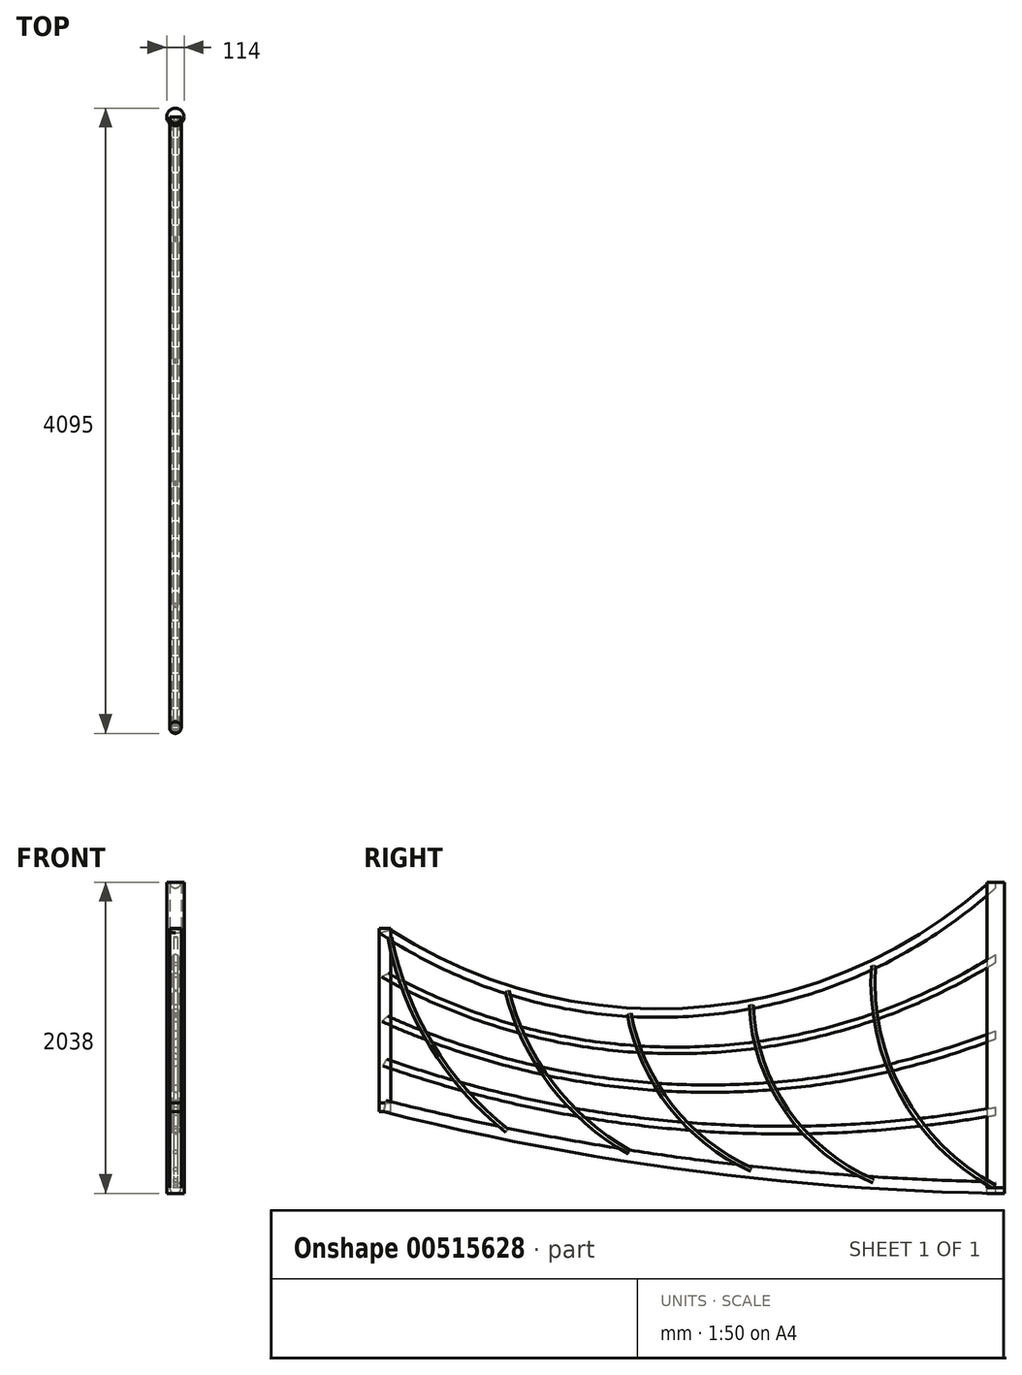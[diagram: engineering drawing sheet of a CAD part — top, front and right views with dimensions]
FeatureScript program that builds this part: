
annotation { "Feature Type Name" : "Feature", "Feature Type Description" : "" }
export const myFeature = defineFeature(function(context is Context, id is Id, definition is map)
    precondition{}
    {
        {
            var Q0;
            Q0=qCreatedBy(makeId("Right.planeOp"),FACE);
            var sketch = newSketch(context, id + "F0", { "sketchPlane" : qUnion([Q0])});
            skLineSegment(sketch, "E0.top", {"start": v(0, 2000) * mm, "end": v(-4000, 2000) * mm});
            skLineSegment(sketch, "E0.left", {"start": v(0, 0) * mm, "end": v(0, 2000) * mm});
            skLineSegment(sketch, "E0.right", {"start": v(-4000, 0) * mm, "end": v(-4000, 2000) * mm});
            skPoint(sketch, "E1", {"position": v(-4000, 533) * mm});
            skPoint(sketch, "E2", {"position": v(-4000, 819) * mm});
            skPoint(sketch, "E3", {"position": v(-4000, 1105) * mm});
            skPoint(sketch, "E4", {"position": v(-4000, 1678) * mm});
            skPoint(sketch, "E5", {"position": v(-4000, 178) * mm});
            skPoint(sketch, "E6", {"position": v(-4000, 1391) * mm});
            skPoint(sketch, "E7", {"position": v(0, 500) * mm});
            skPoint(sketch, "E8", {"position": v(0, 1000) * mm});
            skPoint(sketch, "E9", {"position": v(0, 1500) * mm});
            skPoint(sketch, "E10", {"position": v(0, 2000) * mm});
            skArc(sketch, "E11", {"start": v(-4000, 533) * mm, "mid": v(-2015.3, 151.64) * mm, "end": v(0, 0) * mm});
            skPoint(sketch, "E12", {"position": v(-2000, 0) * mm});
            skPoint(sketch, "E13", {"position": v(-2000, 649.6) * mm});
            skPoint(sketch, "E14", {"position": v(-2000, 899.6) * mm});
            skPoint(sketch, "E15", {"position": v(-2000, 1149.6) * mm});
            skPoint(sketch, "E16", {"position": v(-2000, 399.6) * mm});
            skLineSegment(sketch, "E17", {"start": v(-2000, 0) * mm, "end": v(-2000, 149.6) * mm});
            skArc(sketch, "E18", {"start": v(-4000, 819) * mm, "mid": v(-2020.6, 401.22) * mm, "end": v(0, 500) * mm});
            skArc(sketch, "E19", {"start": v(-4000, 1105) * mm, "mid": v(-2010.57, 649.87) * mm, "end": v(0, 1000) * mm});
            skArc(sketch, "E20", {"start": v(-4000, 1391) * mm, "mid": v(-1985.13, 899.98) * mm, "end": v(0, 1500) * mm});
            skArc(sketch, "E21", {"start": v(-4000, 1678) * mm, "mid": v(-1944.82, 1153.58) * mm, "end": v(0, 2000) * mm});
            skSolve(sketch);
        }
        {
            var Q0;
            Q0=qCreatedBy(makeId("Front.planeOp"),FACE);
            var sketch = newSketch(context, id + "F1", { "sketchPlane" : qUnion([Q0])});
            skCircle(sketch, "E22", {"center": v(0, 0) * mm, "radius": 38 * mm});
            skCircle(sketch, "E23", {"center": v(0, 500) * mm, "radius": 25.5 * mm});
            skCircle(sketch, "E24", {"center": v(0, 1000) * mm, "radius": 25.5 * mm});
            skCircle(sketch, "E25", {"center": v(0, 1500) * mm, "radius": 25.5 * mm});
            skCircle(sketch, "E26", {"center": v(0, 2000) * mm, "radius": 38 * mm});
            skSolve(sketch);
        }
        {
            var Q0;
            Q0=makeQuery(id+"F1.imprint","IMPRINT",FACE,{"disambiguationData":[TD([[makeQuery(id+"F1.imprint","IMPRINT",EDGE,{"derivedFrom":sQuery(id+"F1.wireOp",EDGE,"E22")}),1.0]])]});
            var Q1;
            Q1=sQuery(id+"F0.wireOp",EDGE,"E11");
            sweep(context, id + "F2", {"profiles" : qUnion([Q0]), "path" : qUnion([Q1])});
        }
        {
            var Q0;
            Q0=makeQuery(id+"F1.imprint","IMPRINT",FACE,{"disambiguationData":[TD([[makeQuery(id+"F1.imprint","IMPRINT",EDGE,{"derivedFrom":sQuery(id+"F1.wireOp",EDGE,"E23")}),1.0]])]});
            var Q1;
            Q1=sQuery(id+"F0.wireOp",EDGE,"E18");
            sweep(context, id + "F3", {"profiles" : qUnion([Q0]), "path" : qUnion([Q1])});
        }
        {
            var Q0;
            Q0=makeQuery(id+"F1.imprint","IMPRINT",FACE,{"disambiguationData":[TD([[makeQuery(id+"F1.imprint","IMPRINT",EDGE,{"derivedFrom":sQuery(id+"F1.wireOp",EDGE,"E24")}),1.0]])]});
            var Q1;
            Q1=sQuery(id+"F0.wireOp",EDGE,"E19");
            sweep(context, id + "F4", {"profiles" : qUnion([Q0]), "path" : qUnion([Q1])});
        }
        {
            var Q0;
            Q0=makeQuery(id+"F1.imprint","IMPRINT",FACE,{"disambiguationData":[TD([[makeQuery(id+"F1.imprint","IMPRINT",EDGE,{"derivedFrom":sQuery(id+"F1.wireOp",EDGE,"E25")}),1.0]])]});
            var Q1;
            Q1=sQuery(id+"F0.wireOp",EDGE,"E20");
            sweep(context, id + "F5", {"profiles" : qUnion([Q0]), "path" : qUnion([Q1])});
        }
        {
            var Q0;
            Q0=makeQuery(id+"F1.imprint","IMPRINT",FACE,{"disambiguationData":[TD([[makeQuery(id+"F1.imprint","IMPRINT",EDGE,{"derivedFrom":sQuery(id+"F1.wireOp",EDGE,"E26")}),1.0]])]});
            var Q1;
            Q1=sQuery(id+"F0.wireOp",EDGE,"E21");
            sweep(context, id + "F6", {"profiles" : qUnion([Q0]), "path" : qUnion([Q1])});
        }
        {
            var Q0;
            Q0=qCreatedBy(makeId("Top.planeOp"),FACE);
            var sketch = newSketch(context, id + "F7", { "sketchPlane" : qUnion([Q0])});
            skCircle(sketch, "E27", {"center": v(0, 0) * mm, "radius": 57 * mm});
            skSolve(sketch);
        }
        {
            var Q0;
            Q0=makeQuery(id+"F7.imprint","IMPRINT",FACE,{"disambiguationData":[TD([[makeQuery(id+"F7.imprint","IMPRINT",EDGE,{"derivedFrom":sQuery(id+"F7.wireOp",EDGE,"E27")}),1.0]])]});
            extrude(context, id + "F8", {"entities" : qUnion([Q0]), "depth" : 2000 * mm, "offsetDistance" : 25 * mm});
        }
        {
            var Q0;
            Q0=qCreatedBy(makeId("Top.planeOp"),FACE);
            cPlane(context, id + "F9", {"entities" : qUnion([Q0]), "cplaneType" : CPlaneType.OFFSET, "offset" : 553 * mm, "width" : 150 * mm, "height" : 150 * mm});
        }
        {
            var Q0;
            Q0=qCreatedBy(id+"F9.planeOp",FACE);
            var sketch = newSketch(context, id + "F10", { "sketchPlane" : qUnion([Q0])});
            skCircle(sketch, "E28", {"center": v(0, -4000) * mm, "radius": 38 * mm});
            skSolve(sketch);
        }
        {
            var Q0;
            Q0=makeQuery(id+"F10.imprint","IMPRINT",FACE,{"disambiguationData":[TD([[makeQuery(id+"F10.imprint","IMPRINT",EDGE,{"derivedFrom":sQuery(id+"F10.wireOp",EDGE,"E28")}),1.0]])]});
            extrude(context, id + "F11", {"entities" : qUnion([Q0]), "depth" : 1145 * mm, "offsetDistance" : 25 * mm});
        }
        {
            var Q0;
            Q0=makeQuery(id+"F6.opSweep","CAP_FACE",FACE,{"disambiguationData":[OSD([sQuery(id+"F0.wireOp",VERTEX,"E21.end"),sQuery(id+"F1.wireOp",EDGE,"E26")])],"isStart":true});
            var sketch = newSketch(context, id + "F12", { "sketchPlane" : qUnion([Q0])});
            skLineSegment(sketch, "E29.0", {"start": v(-57, 2000) * mm, "end": v(57, 2000) * mm});
            skLineSegment(sketch, "E30.top", {"start": v(-57, 2046.28) * mm, "end": v(57, 2046.28) * mm});
            skLineSegment(sketch, "E30.left", {"start": v(-57, 2000) * mm, "end": v(-57, 2046.28) * mm});
            skLineSegment(sketch, "E30.right", {"start": v(57, 2000) * mm, "end": v(57, 2046.28) * mm});
            skSolve(sketch);
        }
        {
            var Q0;
            {var subQ0=sQuery(id+"F12.wireOp",EDGE,"E29.0");var subQ1=makeQuery(id+"F6.opSweep","CAP_EDGE",EDGE,{"disambiguationData":[OSD([sQuery(id+"F0.wireOp",VERTEX,"E21.end"),sQuery(id+"F1.wireOp",EDGE,"E26")])],"isStart":true});var subQ2=makeQuery(id+"F12.imprint","INTERSECT",VERTEX,{"disambiguationData":[OD(0.0)],"derivedFrom":[subQ1,subQ0]});Q0=makeQuery(id+"F12.imprint","IMPRINT",FACE,{"disambiguationData":[TD([[makeQuery(id+"F12.imprint","IMPRINT",EDGE,{"disambiguationData":[TD([[subQ2,-1.0]])],"derivedFrom":subQ0}),1.0]])]});}
            extrude(context, id + "F13", {"entities" : qUnion([Q0]), "operationType" : NewBodyOperationType.REMOVE, "oppositeDirection" : true, "depth" : 50 * mm, "offsetDistance" : 25 * mm});
        }
        {
            var Q0;
            Q0=makeQuery(id+"F8.opExtrude","CAP_FACE",FACE,{"disambiguationData":[OSD([sQuery(id+"F7.wireOp",EDGE,"E27")])],"isStart":true});
            extrude(context, id + "F14", {"entities" : qUnion([Q0]), "depth" : 38 * mm, "offsetDistance" : 25 * mm});
        }
        {
            var Q0;
            Q0=makeQuery(id+"F11.opExtrude","CAP_FACE",FACE,{"disambiguationData":[OSD([sQuery(id+"F10.wireOp",EDGE,"E28")])],"isStart":true});
            extrude(context, id + "F15", {"entities" : qUnion([Q0]), "depth" : 57 * mm, "offsetDistance" : 25 * mm});
        }
        {
            var Q0;
            Q0=qCreatedBy(makeId("Right.planeOp"),FACE);
            var sketch = newSketch(context, id + "F16", { "sketchPlane" : qUnion([Q0])});
            skLineSegment(sketch, "E31.bottom", {"start": v(0, 0) * mm, "end": v(-4000, 0) * mm});
            skLineSegment(sketch, "E31.top", {"start": v(0, 2000) * mm, "end": v(-4000, 2000) * mm});
            skLineSegment(sketch, "E31.left", {"start": v(0, 0) * mm, "end": v(0, 2000) * mm});
            skLineSegment(sketch, "E31.right", {"start": v(-4000, 0) * mm, "end": v(-4000, 2000) * mm});
            skPoint(sketch, "E32", {"position": v(-800, 0) * mm});
            skPoint(sketch, "E33", {"position": v(-1600, 0) * mm});
            skPoint(sketch, "E34", {"position": v(-2400, 0) * mm});
            skPoint(sketch, "E35", {"position": v(-3200, 0) * mm});
            skArc(sketch, "E36", {"start": v(-2400, 1139.17) * mm, "mid": v(-2125.18, 530.64) * mm, "end": v(-1600, 118.3) * mm});
            skArc(sketch, "E37", {"start": v(-3200, 1287.54) * mm, "mid": v(-2908.55, 677.52) * mm, "end": v(-2400, 232.05) * mm});
            skArc(sketch, "E38", {"start": v(-3967.74, 1638.29) * mm, "mid": v(-3697.33, 936.32) * mm, "end": v(-3200, 371.92) * mm});
            skArc(sketch, "E39", {"start": v(-800, 1452.85) * mm, "mid": v(-613.16, 609.05) * mm, "end": v(0, 0) * mm});
            skArc(sketch, "E40", {"start": v(-1600, 1195.26) * mm, "mid": v(-1367.03, 503.31) * mm, "end": v(-800, 43.38) * mm});
            skArc(sketch, "E41.0", {"start": v(-812.97, 1453.72) * mm, "mid": v(-624.55, 602.78) * mm, "end": v(-6.2, -11.43) * mm});
            skArc(sketch, "E42.0", {"start": v(-787.03, 1451.97) * mm, "mid": v(-601.78, 615.32) * mm, "end": v(6.2, 11.43) * mm});
            skArc(sketch, "E43.0", {"start": v(-1612.99, 1194.7) * mm, "mid": v(-1377.7, 495.9) * mm, "end": v(-805.05, 31.4) * mm});
            skArc(sketch, "E44.0", {"start": v(-1587.01, 1195.81) * mm, "mid": v(-1356.35, 510.73) * mm, "end": v(-794.95, 55.36) * mm});
            skArc(sketch, "E45.0", {"start": v(-2412.78, 1136.8) * mm, "mid": v(-2135.4, 522.62) * mm, "end": v(-1605.36, 106.45) * mm});
            skArc(sketch, "E46.0", {"start": v(-2387.22, 1141.54) * mm, "mid": v(-2114.94, 538.65) * mm, "end": v(-1594.64, 130.13) * mm});
            skArc(sketch, "E47.0", {"start": v(-3212.62, 1284.41) * mm, "mid": v(-2918.9, 669.67) * mm, "end": v(-2406.42, 220.75) * mm});
            skArc(sketch, "E48.0", {"start": v(-3187.38, 1290.66) * mm, "mid": v(-2898.19, 685.37) * mm, "end": v(-2393.58, 243.35) * mm});
            skArc(sketch, "E49.0", {"start": v(-3980.5, 1635.83) * mm, "mid": v(-3708.45, 929.58) * mm, "end": v(-3208.08, 361.74) * mm});
            skArc(sketch, "E50.0", {"start": v(-3954.98, 1640.75) * mm, "mid": v(-3686.22, 943.06) * mm, "end": v(-3191.92, 382.1) * mm});
            skLineSegment(sketch, "E51", {"start": v(-3208.08, 361.74) * mm, "end": v(-3191.92, 382.1) * mm});
            skLineSegment(sketch, "E52", {"start": v(-2406.42, 220.75) * mm, "end": v(-2393.58, 243.35) * mm});
            skLineSegment(sketch, "E53", {"start": v(-1605.36, 106.45) * mm, "end": v(-1594.64, 130.13) * mm});
            skLineSegment(sketch, "E54", {"start": v(-805.05, 31.4) * mm, "end": v(-794.95, 55.36) * mm});
            skLineSegment(sketch, "E55", {"start": v(-6.2, -11.43) * mm, "end": v(6.2, 11.43) * mm});
            skLineSegment(sketch, "E56", {"start": v(-787.03, 1451.97) * mm, "end": v(-812.97, 1453.72) * mm});
            skLineSegment(sketch, "E57", {"start": v(-1587.01, 1195.81) * mm, "end": v(-1612.99, 1194.7) * mm});
            skLineSegment(sketch, "E58", {"start": v(-2387.22, 1141.54) * mm, "end": v(-2412.78, 1136.8) * mm});
            skLineSegment(sketch, "E59", {"start": v(-3187.38, 1290.66) * mm, "end": v(-3212.62, 1284.41) * mm});
            skLineSegment(sketch, "E60", {"start": v(-3954.98, 1640.75) * mm, "end": v(-3980.5, 1635.83) * mm});
            skSolve(sketch);
        }
        {
            var Q0;
            {var subQ0=sQuery(id+"F16.wireOp",EDGE,"E39");Q0=makeQuery(id+"F16.imprint","IMPRINT",FACE,{"disambiguationData":[TD([[makeQuery(id+"F16.imprint","IMPRINT",EDGE,{"derivedFrom":subQ0}),1.0]])]});}
            var Q1;
            {var subQ0=sQuery(id+"F16.wireOp",EDGE,"E39");Q1=makeQuery(id+"F16.imprint","IMPRINT",FACE,{"disambiguationData":[TD([[makeQuery(id+"F16.imprint","IMPRINT",EDGE,{"derivedFrom":subQ0}),-1.0]])]});}
            var Q2;
            {var subQ0=sQuery(id+"F16.wireOp",EDGE,"E40");Q2=makeQuery(id+"F16.imprint","IMPRINT",FACE,{"disambiguationData":[TD([[makeQuery(id+"F16.imprint","IMPRINT",EDGE,{"derivedFrom":subQ0}),1.0]])]});}
            var Q3;
            {var subQ0=sQuery(id+"F16.wireOp",EDGE,"E40");Q3=makeQuery(id+"F16.imprint","IMPRINT",FACE,{"disambiguationData":[TD([[makeQuery(id+"F16.imprint","IMPRINT",EDGE,{"derivedFrom":subQ0}),-1.0]])]});}
            var Q4;
            {var subQ0=sQuery(id+"F16.wireOp",EDGE,"E36");Q4=makeQuery(id+"F16.imprint","IMPRINT",FACE,{"disambiguationData":[TD([[makeQuery(id+"F16.imprint","IMPRINT",EDGE,{"derivedFrom":subQ0}),1.0]])]});}
            var Q5;
            {var subQ0=sQuery(id+"F16.wireOp",EDGE,"E36");Q5=makeQuery(id+"F16.imprint","IMPRINT",FACE,{"disambiguationData":[TD([[makeQuery(id+"F16.imprint","IMPRINT",EDGE,{"derivedFrom":subQ0}),-1.0]])]});}
            var Q6;
            {var subQ0=sQuery(id+"F16.wireOp",EDGE,"E37");Q6=makeQuery(id+"F16.imprint","IMPRINT",FACE,{"disambiguationData":[TD([[makeQuery(id+"F16.imprint","IMPRINT",EDGE,{"derivedFrom":subQ0}),1.0]])]});}
            var Q7;
            {var subQ0=sQuery(id+"F16.wireOp",EDGE,"E37");Q7=makeQuery(id+"F16.imprint","IMPRINT",FACE,{"disambiguationData":[TD([[makeQuery(id+"F16.imprint","IMPRINT",EDGE,{"derivedFrom":subQ0}),-1.0]])]});}
            var Q8;
            {var subQ0=sQuery(id+"F16.wireOp",EDGE,"E38");Q8=makeQuery(id+"F16.imprint","IMPRINT",FACE,{"disambiguationData":[TD([[makeQuery(id+"F16.imprint","IMPRINT",EDGE,{"derivedFrom":subQ0}),1.0]])]});}
            var Q9;
            {var subQ0=sQuery(id+"F16.wireOp",EDGE,"E38");Q9=makeQuery(id+"F16.imprint","IMPRINT",FACE,{"disambiguationData":[TD([[makeQuery(id+"F16.imprint","IMPRINT",EDGE,{"derivedFrom":subQ0}),-1.0]])]});}
            extrude(context, id + "F17", {"entities" : qUnion([Q0, Q1, Q2, Q3, Q4, Q5, Q6, Q7, Q8, Q9]), "endBound" : BoundingType.SYMMETRIC, "depth" : 25 * mm, "offsetDistance" : 25 * mm});
        }
    });
